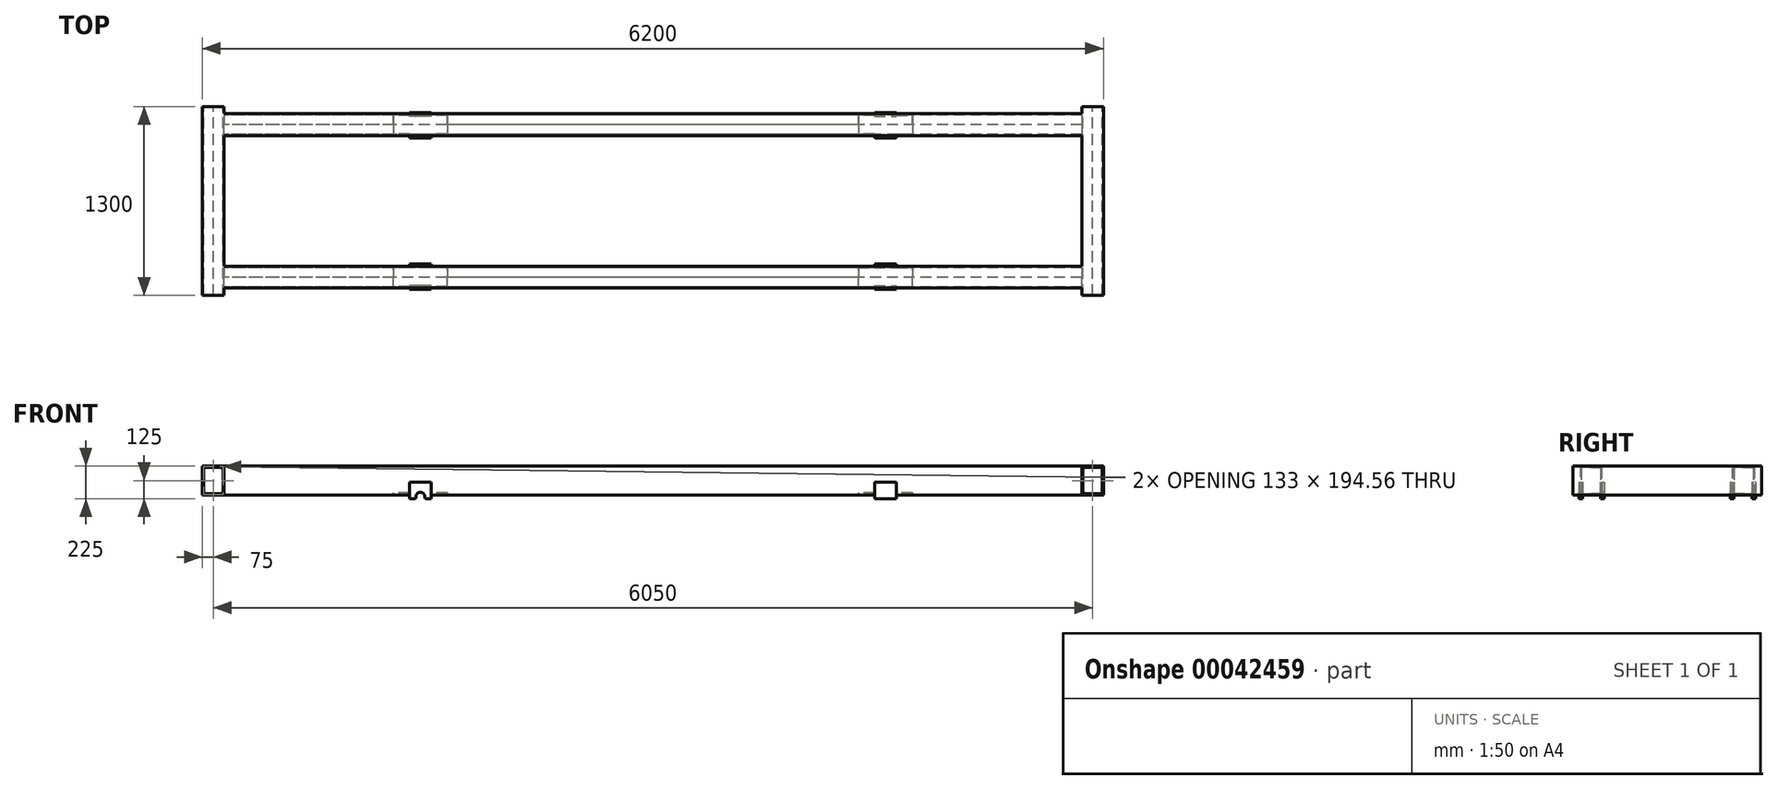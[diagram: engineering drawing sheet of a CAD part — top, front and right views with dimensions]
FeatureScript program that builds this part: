
annotation { "Feature Type Name" : "Feature", "Feature Type Description" : "" }
export const myFeature = defineFeature(function(context is Context, id is Id, definition is map)
    precondition{}
    {
        {
            assignVariable(context, id + "F0", {"variableType" : VariableType.LENGTH, "name" : "ProduktL", "lengthValue" : 6000 * mm});
        }
        {
            assignVariable(context, id + "F1", {"variableType" : VariableType.LENGTH, "name" : "ProduktB", "lengthValue" : 1300 * mm});
        }
        {
            assignVariable(context, id + "F2", {"variableType" : VariableType.LENGTH, "name" : "Spurweite", "lengthValue" : 1000 * mm});
        }
        {
            var Q0;
            Q0=qCreatedBy(makeId("Right.planeOp"),FACE);
            var sketch = newSketch(context, id + "F3", { "sketchPlane" : qUnion([Q0])});
            skLineSegment(sketch, "E0", {"start": v(-525, -69.6) * mm, "end": v(-525, -185.96) * mm, "construction": true});
            skLineSegment(sketch, "E1", {"start": v(-562.5, 183.56) * mm, "end": v(-562.5, -200) * mm, "construction": true});
            skLineSegment(sketch, "E2", {"start": v(-525, -100) * mm, "end": v(-600, -100) * mm, "construction": true});
            skLineSegment(sketch, "E3", {"start": v(-525, -2.72) * mm, "end": v(-525, 0) * mm});
            skPoint(sketch, "E3.startSnap0", {"position": v(-562.5, -8.22) * mm});
            skLineSegment(sketch, "E4", {"start": v(-525, 0) * mm, "end": v(-600, 0) * mm});
            skLineSegment(sketch, "E5", {"start": v(-600, 0) * mm, "end": v(-600, -200) * mm});
            skLineSegment(sketch, "E6", {"start": v(-600, -200) * mm, "end": v(-525, -200) * mm});
            skLineSegment(sketch, "E7", {"start": v(-525, -200) * mm, "end": v(-525, -197.28) * mm});
            skLineSegment(sketch, "E8", {"start": v(-530.48, -191.3) * mm, "end": v(-586.02, -186.44) * mm});
            skLineSegment(sketch, "E9", {"start": v(-591.5, -180.46) * mm, "end": v(-591.5, -19.54) * mm});
            skLineSegment(sketch, "E10", {"start": v(-586.02, -13.56) * mm, "end": v(-530.48, -8.7) * mm});
            skPoint(sketch, "E11.visualSharp", {"position": v(-591.5, -14.04) * mm});
            skArc(sketch, "E11.filletArc", {"start": v(-586.02, -13.56) * mm, "mid": v(-589.92, -15.48) * mm, "end": v(-591.5, -19.54) * mm});
            skPoint(sketch, "E12.visualSharp", {"position": v(-525, -8.22) * mm});
            skArc(sketch, "E12.filletArc", {"start": v(-530.48, -8.7) * mm, "mid": v(-526.58, -6.77) * mm, "end": v(-525, -2.72) * mm});
            skPoint(sketch, "E13.visualSharp", {"position": v(-525, -191.78) * mm});
            skArc(sketch, "E13.filletArc", {"start": v(-525, -197.28) * mm, "mid": v(-526.58, -193.23) * mm, "end": v(-530.48, -191.3) * mm});
            skPoint(sketch, "E14.visualSharp", {"position": v(-591.5, -185.96) * mm});
            skArc(sketch, "E14.filletArc", {"start": v(-591.5, -180.46) * mm, "mid": v(-589.92, -184.52) * mm, "end": v(-586.02, -186.44) * mm});
            skPoint(sketch, "E15", {"position": v(-600, -100) * mm});
            skPoint(sketch, "E16", {"position": v(-562.5, -200) * mm});
            skLineSegment(sketch, "E17", {"start": v(-562.5, 0) * mm, "end": v(-562.5, -11.5) * mm, "construction": true});
            skPoint(sketch, "E18", {"position": v(-591.5, -100) * mm});
            skLineSegment(sketch, "E19", {"start": v(-500, 0) * mm, "end": v(500, 0) * mm, "construction": true});
            skPoint(sketch, "E20", {"position": v(0, 0) * mm});
            skArc(sketch, "E21.MirrorCS", {"start": v(-525, -197.28) * mm, "mid": v(-523.42, -193.23) * mm, "end": v(-519.52, -191.3) * mm});
            skArc(sketch, "E22.MirrorCS", {"start": v(-458.5, -180.46) * mm, "mid": v(-460.08, -184.52) * mm, "end": v(-463.98, -186.44) * mm});
            skArc(sketch, "E23.MirrorCS", {"start": v(-463.98, -13.56) * mm, "mid": v(-460.08, -15.48) * mm, "end": v(-458.5, -19.54) * mm});
            skArc(sketch, "E24.MirrorCS", {"start": v(-519.52, -8.7) * mm, "mid": v(-523.42, -6.77) * mm, "end": v(-525, -2.72) * mm});
            skLineSegment(sketch, "E25.MirrorCS", {"start": v(-487.5, 0) * mm, "end": v(-487.5, -11.5) * mm, "construction": true});
            skPoint(sketch, "E26.MirrorP", {"position": v(-487.5, -8.22) * mm});
            skLineSegment(sketch, "E27.MirrorCS", {"start": v(-450, -200) * mm, "end": v(-525, -200) * mm});
            skLineSegment(sketch, "E28.MirrorCS", {"start": v(-458.5, -180.46) * mm, "end": v(-458.5, -19.54) * mm});
            skPoint(sketch, "E29.MirrorP", {"position": v(-458.5, -14.04) * mm});
            skLineSegment(sketch, "E30.MirrorCS", {"start": v(-525, -100) * mm, "end": v(-450, -100) * mm, "construction": true});
            skPoint(sketch, "E31.MirrorP", {"position": v(-450, -100) * mm});
            skLineSegment(sketch, "E32.MirrorCS", {"start": v(-519.52, -191.3) * mm, "end": v(-463.98, -186.44) * mm});
            skPoint(sketch, "E33.MirrorP", {"position": v(-458.5, -185.96) * mm});
            skPoint(sketch, "E34.MirrorP", {"position": v(-458.5, -100) * mm});
            skLineSegment(sketch, "E35.MirrorCS", {"start": v(-525, 0) * mm, "end": v(-450, 0) * mm});
            skLineSegment(sketch, "E36.MirrorCS", {"start": v(-463.98, -13.56) * mm, "end": v(-519.52, -8.7) * mm});
            skLineSegment(sketch, "E37.MirrorCS", {"start": v(-450, 0) * mm, "end": v(-450, -200) * mm});
            skPoint(sketch, "E38.MirrorP", {"position": v(-487.5, -200) * mm});
            skLineSegment(sketch, "E39.MirrorCS", {"start": v(525, -200) * mm, "end": v(525, -197.28) * mm});
            skArc(sketch, "E40.MirrorCS", {"start": v(525, -197.28) * mm, "mid": v(523.42, -193.23) * mm, "end": v(519.52, -191.3) * mm});
            skLineSegment(sketch, "E41.MirrorCS", {"start": v(525, -2.72) * mm, "end": v(525, 0) * mm});
            skArc(sketch, "E42.MirrorCS", {"start": v(525, -197.28) * mm, "mid": v(526.58, -193.23) * mm, "end": v(530.48, -191.3) * mm});
            skArc(sketch, "E43.MirrorCS", {"start": v(519.52, -8.7) * mm, "mid": v(523.42, -6.77) * mm, "end": v(525, -2.72) * mm});
            skArc(sketch, "E44.MirrorCS", {"start": v(530.48, -8.7) * mm, "mid": v(526.58, -6.77) * mm, "end": v(525, -2.72) * mm});
            skArc(sketch, "E45.MirrorCS", {"start": v(463.98, -13.56) * mm, "mid": v(460.08, -15.48) * mm, "end": v(458.5, -19.54) * mm});
            skArc(sketch, "E46.MirrorCS", {"start": v(591.5, -180.46) * mm, "mid": v(589.92, -184.52) * mm, "end": v(586.02, -186.44) * mm});
            skArc(sketch, "E47.MirrorCS", {"start": v(586.02, -13.56) * mm, "mid": v(589.92, -15.48) * mm, "end": v(591.5, -19.54) * mm});
            skArc(sketch, "E48.MirrorCS", {"start": v(458.5, -180.46) * mm, "mid": v(460.08, -184.52) * mm, "end": v(463.98, -186.44) * mm});
            skLineSegment(sketch, "E49.MirrorCS", {"start": v(586.02, -13.56) * mm, "end": v(530.48, -8.7) * mm});
            skPoint(sketch, "E50.MirrorP", {"position": v(525, -8.22) * mm});
            skPoint(sketch, "E51.MirrorP", {"position": v(525, -191.78) * mm});
            skLineSegment(sketch, "E52.MirrorCS", {"start": v(487.5, 0) * mm, "end": v(487.5, -11.5) * mm, "construction": true});
            skLineSegment(sketch, "E53.MirrorCS", {"start": v(562.5, 0) * mm, "end": v(562.5, -11.5) * mm, "construction": true});
            skLineSegment(sketch, "E54.MirrorCS", {"start": v(458.5, -180.46) * mm, "end": v(458.5, -19.54) * mm});
            skPoint(sketch, "E55.MirrorP", {"position": v(458.5, -14.04) * mm});
            skLineSegment(sketch, "E56.MirrorCS", {"start": v(525, 0) * mm, "end": v(600, 0) * mm});
            skPoint(sketch, "E57.MirrorP", {"position": v(591.5, -100) * mm});
            skLineSegment(sketch, "E58.MirrorCS", {"start": v(519.52, -191.3) * mm, "end": v(463.98, -186.44) * mm});
            skLineSegment(sketch, "E59.MirrorCS", {"start": v(525, 0) * mm, "end": v(450, 0) * mm});
            skLineSegment(sketch, "E60.MirrorCS", {"start": v(450, 0) * mm, "end": v(450, -200) * mm});
            skLineSegment(sketch, "E61.MirrorCS", {"start": v(525, -100) * mm, "end": v(450, -100) * mm, "construction": true});
            skPoint(sketch, "E62.MirrorP", {"position": v(458.5, -185.96) * mm});
            skPoint(sketch, "E63.MirrorP", {"position": v(591.5, -185.96) * mm});
            skPoint(sketch, "E64.MirrorP", {"position": v(562.5, -8.22) * mm});
            skLineSegment(sketch, "E65.MirrorCS", {"start": v(530.48, -191.3) * mm, "end": v(586.02, -186.44) * mm});
            skLineSegment(sketch, "E66.MirrorCS", {"start": v(600, 0) * mm, "end": v(600, -200) * mm});
            skLineSegment(sketch, "E67.MirrorCS", {"start": v(600, -200) * mm, "end": v(525, -200) * mm});
            skLineSegment(sketch, "E68.MirrorCS", {"start": v(591.5, -180.46) * mm, "end": v(591.5, -19.54) * mm});
            skPoint(sketch, "E69.MirrorP", {"position": v(450, -100) * mm});
            skLineSegment(sketch, "E70.MirrorCS", {"start": v(450, -200) * mm, "end": v(525, -200) * mm});
            skPoint(sketch, "E71.MirrorP", {"position": v(562.5, -200) * mm});
            skPoint(sketch, "E72.MirrorP", {"position": v(600, -100) * mm});
            skPoint(sketch, "E73.MirrorP", {"position": v(487.5, -200) * mm});
            skPoint(sketch, "E74.MirrorP", {"position": v(591.5, -14.04) * mm});
            skLineSegment(sketch, "E75.MirrorCS", {"start": v(525, -69.6) * mm, "end": v(525, -185.96) * mm, "construction": true});
            skLineSegment(sketch, "E76.MirrorCS", {"start": v(525, -100) * mm, "end": v(600, -100) * mm, "construction": true});
            skPoint(sketch, "E77.MirrorP", {"position": v(458.5, -100) * mm});
            skLineSegment(sketch, "E78.MirrorCS", {"start": v(463.98, -13.56) * mm, "end": v(519.52, -8.7) * mm});
            skPoint(sketch, "E79.MirrorP", {"position": v(487.5, -8.22) * mm});
            skSolve(sketch);
        }
        {
            var Q0;
            Q0=makeQuery(id+"F3.imprint","IMPRINT",FACE,{"disambiguationData":[TD([[makeQuery(id+"F3.imprint","IMPRINT",EDGE,{"derivedFrom":sQuery(id+"F3.wireOp",EDGE,"E4")}),1.0]])]});
            var Q1;
            Q1=makeQuery(id+"F3.imprint","IMPRINT",FACE,{"disambiguationData":[TD([[makeQuery(id+"F3.imprint","IMPRINT",EDGE,{"derivedFrom":sQuery(id+"F3.wireOp",EDGE,"E7")}),-1.0]])]});
            var Q2;
            Q2=makeQuery(id+"F3.imprint","IMPRINT",FACE,{"disambiguationData":[TD([[makeQuery(id+"F3.imprint","IMPRINT",EDGE,{"derivedFrom":sQuery(id+"F3.wireOp",EDGE,"E39.MirrorCS")}),1.0]])]});
            var Q3;
            Q3=makeQuery(id+"F3.imprint","IMPRINT",FACE,{"disambiguationData":[TD([[makeQuery(id+"F3.imprint","IMPRINT",EDGE,{"derivedFrom":sQuery(id+"F3.wireOp",EDGE,"E39.MirrorCS")}),-1.0]])]});
            extrude(context, id + "F4", {"entities" : qUnion([Q0, Q1, Q2, Q3]), "endBound" : BoundingType.SYMMETRIC, "depth" : getVariable(context, 'ProduktL'), "offsetDistance" : 25 * mm});
        }
        {
            var Q0;
            Q0=makeQuery(id+"F4.opExtrude","SWEPT_FACE",FACE,{"disambiguationData":[OSD([sQuery(id+"F3.wireOp",EDGE,"E5")])]});
            var sketch = newSketch(context, id + "F5", { "sketchPlane" : qUnion([Q0])});
            skLineSegment(sketch, "E80", {"start": v(-3000, 0) * mm, "end": v(3000, 0) * mm, "construction": true});
            skPoint(sketch, "E81", {"position": v(0, 0) * mm});
            skLineSegment(sketch, "E82", {"start": v(-3000, 0) * mm, "end": v(-3100, 0) * mm, "construction": true});
            skLineSegment(sketch, "E83", {"start": v(3000, 0) * mm, "end": v(3100, 0) * mm, "construction": true});
            skLineSegment(sketch, "E84.bottom", {"start": v(-3100, 0) * mm, "end": v(-3025, 0) * mm});
            skLineSegment(sketch, "E84.top", {"start": v(-3100, -200) * mm, "end": v(-3025, -200) * mm});
            skLineSegment(sketch, "E84.left", {"start": v(-3100, 0) * mm, "end": v(-3100, -200) * mm});
            skLineSegment(sketch, "E84.right", {"start": v(-3025, 0) * mm, "end": v(-3025, -200) * mm});
            skLineSegment(sketch, "E85.bottom", {"start": v(-3025, 0) * mm, "end": v(-2950, 0) * mm});
            skLineSegment(sketch, "E85.top", {"start": v(-3025, -200) * mm, "end": v(-2950, -200) * mm});
            skLineSegment(sketch, "E85.right", {"start": v(-2950, 0) * mm, "end": v(-2950, -200) * mm});
            skLineSegment(sketch, "E86.MirrorCS", {"start": v(3025, 0) * mm, "end": v(3025, -200) * mm});
            skLineSegment(sketch, "E87.MirrorCS", {"start": v(3100, 0) * mm, "end": v(3025, 0) * mm});
            skLineSegment(sketch, "E88.MirrorCS", {"start": v(3100, 0) * mm, "end": v(3100, -200) * mm});
            skLineSegment(sketch, "E89.MirrorCS", {"start": v(3025, 0) * mm, "end": v(2950, 0) * mm});
            skLineSegment(sketch, "E90.MirrorCS", {"start": v(2950, 0) * mm, "end": v(2950, -200) * mm});
            skLineSegment(sketch, "E91.MirrorCS", {"start": v(3025, -200) * mm, "end": v(2950, -200) * mm});
            skLineSegment(sketch, "E92.MirrorCS", {"start": v(3100, -200) * mm, "end": v(3025, -200) * mm});
            skSolve(sketch);
        }
        {
            var Q0;
            Q0=makeQuery(id+"F5.imprint","IMPRINT",FACE,{"disambiguationData":[TD([[makeQuery(id+"F5.imprint","IMPRINT",EDGE,{"derivedFrom":sQuery(id+"F5.wireOp",EDGE,"E84.bottom")}),-1.0]])]});
            var Q1;
            {var subQ3=sQuery(id+"F5.wireOp",EDGE,"E85.right");Q1=makeQuery(id+"F5.imprint","IMPRINT",FACE,{"disambiguationData":[TD([[makeQuery(id+"F5.imprint","IMPRINT",EDGE,{"derivedFrom":subQ3}),-1.0]])]});}
            var Q2;
            {var subQ0=sQuery(id+"F5.wireOp",EDGE,"E86.MirrorCS");Q2=makeQuery(id+"F5.imprint","IMPRINT",FACE,{"disambiguationData":[TD([[makeQuery(id+"F5.imprint","IMPRINT",EDGE,{"derivedFrom":subQ0}),-1.0]])]});}
            var Q3;
            {var subQ3=sQuery(id+"F5.wireOp",EDGE,"E90.MirrorCS");Q3=makeQuery(id+"F5.imprint","IMPRINT",FACE,{"disambiguationData":[TD([[makeQuery(id+"F5.imprint","IMPRINT",EDGE,{"derivedFrom":subQ3}),1.0]])]});}
            var Q4;
            Q4=makeQuery(id+"F5.imprint","IMPRINT",FACE,{"disambiguationData":[TD([[makeQuery(id+"F5.imprint","IMPRINT",EDGE,{"derivedFrom":sQuery(id+"F5.wireOp",EDGE,"E87.MirrorCS")}),1.0]])]});
            var Q5;
            {var subQ2=sQuery(id+"F5.wireOp",EDGE,"E84.right");Q5=makeQuery(id+"F5.imprint","IMPRINT",FACE,{"disambiguationData":[TD([[makeQuery(id+"F5.imprint","IMPRINT",EDGE,{"derivedFrom":subQ2}),1.0]])]});}
            extrude(context, id + "F6", {"entities" : qUnion([Q0, Q1, Q2, Q3, Q4, Q5]), "operationType" : NewBodyOperationType.REMOVE, "endBound" : BoundingType.THROUGH_ALL, "oppositeDirection" : true, "depth" : 25 * mm, "offsetDistance" : 25 * mm});
        }
        {
            var Q0;
            Q0=qCreatedBy(makeId("Front.planeOp"),FACE);
            var sketch = newSketch(context, id + "F7", { "sketchPlane" : qUnion([Q0])});
            skLineSegment(sketch, "E93.0", {"start": v(-2950, -200) * mm, "end": v(-2950, 0) * mm});
            skLineSegment(sketch, "E94", {"start": v(-2950, 0) * mm, "end": v(-3025, 0) * mm});
            skLineSegment(sketch, "E95", {"start": v(-3025, 0) * mm, "end": v(-3025, -2.72) * mm});
            skLineSegment(sketch, "E96", {"start": v(-3019.52, -8.7) * mm, "end": v(-2969, -13.12) * mm});
            skLineSegment(sketch, "E97", {"start": v(-2958.5, -24.57) * mm, "end": v(-2958.5, -175.43) * mm});
            skLineSegment(sketch, "E98", {"start": v(-2969, -186.88) * mm, "end": v(-3019.52, -191.3) * mm});
            skLineSegment(sketch, "E99", {"start": v(-3025, -197.28) * mm, "end": v(-3025, -200) * mm});
            skLineSegment(sketch, "E100", {"start": v(-3025, -200) * mm, "end": v(-2950, -200) * mm});
            skPoint(sketch, "E101.visualSharp", {"position": v(-3025, -8.22) * mm});
            skArc(sketch, "E101.filletArc", {"start": v(-3025, -2.72) * mm, "mid": v(-3023.42, -6.77) * mm, "end": v(-3019.52, -8.7) * mm});
            skPoint(sketch, "E102.visualSharp", {"position": v(-2958.5, -14.04) * mm});
            skArc(sketch, "E102.filletArc", {"start": v(-2958.5, -24.57) * mm, "mid": v(-2961.52, -16.8) * mm, "end": v(-2969, -13.12) * mm});
            skPoint(sketch, "E103.visualSharp", {"position": v(-2958.5, -185.96) * mm});
            skArc(sketch, "E103.filletArc", {"start": v(-2969, -186.88) * mm, "mid": v(-2961.52, -183.2) * mm, "end": v(-2958.5, -175.43) * mm});
            skPoint(sketch, "E104.visualSharp", {"position": v(-3025, -191.78) * mm});
            skArc(sketch, "E104.filletArc", {"start": v(-3019.52, -191.3) * mm, "mid": v(-3023.42, -193.23) * mm, "end": v(-3025, -197.28) * mm});
            skLineSegment(sketch, "E105", {"start": v(-2987.5, 0) * mm, "end": v(-2987.5, -11.5) * mm, "construction": true});
            skLineSegment(sketch, "E106", {"start": v(-3025, 9.58) * mm, "end": v(-3025, 59.58) * mm, "construction": true});
            skArc(sketch, "E107.MirrorCS", {"start": v(-3025, -2.72) * mm, "mid": v(-3026.58, -6.77) * mm, "end": v(-3030.48, -8.7) * mm});
            skArc(sketch, "E108.MirrorCS", {"start": v(-3030.48, -191.3) * mm, "mid": v(-3026.58, -193.23) * mm, "end": v(-3025, -197.28) * mm});
            skArc(sketch, "E109.MirrorCS", {"start": v(-3081, -186.88) * mm, "mid": v(-3088.48, -183.2) * mm, "end": v(-3091.5, -175.43) * mm});
            skLineSegment(sketch, "E110.MirrorCS", {"start": v(-3062.5, 0) * mm, "end": v(-3062.5, -11.5) * mm, "construction": true});
            skArc(sketch, "E111.MirrorCS", {"start": v(-3091.5, -24.57) * mm, "mid": v(-3088.48, -16.8) * mm, "end": v(-3081, -13.12) * mm});
            skLineSegment(sketch, "E112.MirrorCS", {"start": v(-3025, -200) * mm, "end": v(-3100, -200) * mm});
            skLineSegment(sketch, "E113.MirrorCS", {"start": v(-3030.48, -8.7) * mm, "end": v(-3081, -13.12) * mm});
            skLineSegment(sketch, "E114.MirrorCS", {"start": v(-3100, -200) * mm, "end": v(-3100, 0) * mm});
            skLineSegment(sketch, "E115.MirrorCS", {"start": v(-3081, -186.88) * mm, "end": v(-3030.48, -191.3) * mm});
            skLineSegment(sketch, "E116.MirrorCS", {"start": v(-3100, 0) * mm, "end": v(-3025, 0) * mm});
            skPoint(sketch, "E117.MirrorP", {"position": v(-3091.5, -185.96) * mm});
            skLineSegment(sketch, "E118.MirrorCS", {"start": v(-3091.5, -24.57) * mm, "end": v(-3091.5, -175.43) * mm});
            skPoint(sketch, "E119.MirrorP", {"position": v(-3091.5, -14.04) * mm});
            skLineSegment(sketch, "E120.MirrorCS", {"start": v(3025, 0) * mm, "end": v(3025, -2.72) * mm});
            skArc(sketch, "E121.MirrorCS", {"start": v(3025, -2.72) * mm, "mid": v(3026.58, -6.77) * mm, "end": v(3030.48, -8.7) * mm});
            skArc(sketch, "E122.MirrorCS", {"start": v(3025, -2.72) * mm, "mid": v(3023.42, -6.77) * mm, "end": v(3019.52, -8.7) * mm});
            skLineSegment(sketch, "E123.MirrorCS", {"start": v(3025, -197.28) * mm, "end": v(3025, -200) * mm});
            skArc(sketch, "E124.MirrorCS", {"start": v(3030.48, -191.3) * mm, "mid": v(3026.58, -193.23) * mm, "end": v(3025, -197.28) * mm});
            skArc(sketch, "E125.MirrorCS", {"start": v(3019.52, -191.3) * mm, "mid": v(3023.42, -193.23) * mm, "end": v(3025, -197.28) * mm});
            skArc(sketch, "E126.MirrorCS", {"start": v(3081, -186.88) * mm, "mid": v(3088.48, -183.2) * mm, "end": v(3091.5, -175.43) * mm});
            skLineSegment(sketch, "E127.MirrorCS", {"start": v(3062.5, 0) * mm, "end": v(3062.5, -11.5) * mm, "construction": true});
            skLineSegment(sketch, "E128.MirrorCS", {"start": v(2969, -186.88) * mm, "end": v(3019.52, -191.3) * mm});
            skArc(sketch, "E129.MirrorCS", {"start": v(3091.5, -24.57) * mm, "mid": v(3088.48, -16.8) * mm, "end": v(3081, -13.12) * mm});
            skLineSegment(sketch, "E130.MirrorCS", {"start": v(3025, -200) * mm, "end": v(3100, -200) * mm});
            skLineSegment(sketch, "E131.MirrorCS", {"start": v(3019.52, -8.7) * mm, "end": v(2969, -13.12) * mm});
            skLineSegment(sketch, "E132.MirrorCS", {"start": v(2950, 0) * mm, "end": v(3025, 0) * mm});
            skLineSegment(sketch, "E133.MirrorCS", {"start": v(3030.48, -8.7) * mm, "end": v(3081, -13.12) * mm});
            skLineSegment(sketch, "E134.MirrorCS", {"start": v(3081, -186.88) * mm, "end": v(3030.48, -191.3) * mm});
            skArc(sketch, "E135.MirrorCS", {"start": v(2969, -186.88) * mm, "mid": v(2961.52, -183.2) * mm, "end": v(2958.5, -175.43) * mm});
            skLineSegment(sketch, "E136.MirrorCS", {"start": v(3100, 0) * mm, "end": v(3025, 0) * mm});
            skArc(sketch, "E137.MirrorCS", {"start": v(2958.5, -24.57) * mm, "mid": v(2961.52, -16.8) * mm, "end": v(2969, -13.12) * mm});
            skLineSegment(sketch, "E138.MirrorCS", {"start": v(3025, -200) * mm, "end": v(2950, -200) * mm});
            skLineSegment(sketch, "E139.MirrorCS", {"start": v(2987.5, 0) * mm, "end": v(2987.5, -11.5) * mm, "construction": true});
            skPoint(sketch, "E140.MirrorP", {"position": v(3025, -8.22) * mm});
            skPoint(sketch, "E141.MirrorP", {"position": v(3025, -191.78) * mm});
            skPoint(sketch, "E142.MirrorP", {"position": v(2958.5, -185.96) * mm});
            skPoint(sketch, "E143.MirrorP", {"position": v(2958.5, -14.04) * mm});
            skLineSegment(sketch, "E144.MirrorCS", {"start": v(2958.5, -24.57) * mm, "end": v(2958.5, -175.43) * mm});
            skLineSegment(sketch, "E145.MirrorCS", {"start": v(2950, -200) * mm, "end": v(2950, 0) * mm});
            skLineSegment(sketch, "E146.MirrorCS", {"start": v(3091.5, -24.57) * mm, "end": v(3091.5, -175.43) * mm});
            skLineSegment(sketch, "E147.MirrorCS", {"start": v(3100, -200) * mm, "end": v(3100, 0) * mm});
            skPoint(sketch, "E148.MirrorP", {"position": v(3091.5, -185.96) * mm});
            skPoint(sketch, "E149.MirrorP", {"position": v(3091.5, -14.04) * mm});
            skSolve(sketch);
        }
        {
            var Q0;
            Q0=makeQuery(id+"F7.imprint","IMPRINT",FACE,{"disambiguationData":[TD([[makeQuery(id+"F7.imprint","IMPRINT",EDGE,{"derivedFrom":sQuery(id+"F7.wireOp",EDGE,"E99")}),-1.0]])]});
            var Q1;
            Q1=makeQuery(id+"F7.imprint","IMPRINT",FACE,{"disambiguationData":[TD([[makeQuery(id+"F7.imprint","IMPRINT",EDGE,{"derivedFrom":sQuery(id+"F7.wireOp",EDGE,"E93.0")}),1.0]])]});
            var Q2;
            Q2=makeQuery(id+"F7.imprint","IMPRINT",FACE,{"disambiguationData":[TD([[makeQuery(id+"F7.imprint","IMPRINT",EDGE,{"derivedFrom":sQuery(id+"F7.wireOp",EDGE,"E120.MirrorCS")}),-1.0]])]});
            var Q3;
            Q3=makeQuery(id+"F7.imprint","IMPRINT",FACE,{"disambiguationData":[TD([[makeQuery(id+"F7.imprint","IMPRINT",EDGE,{"derivedFrom":sQuery(id+"F7.wireOp",EDGE,"E120.MirrorCS")}),1.0]])]});
            extrude(context, id + "F8", {"entities" : qUnion([Q0, Q1, Q2, Q3]), "operationType" : NewBodyOperationType.ADD, "endBound" : BoundingType.SYMMETRIC, "depth" : getVariable(context, 'ProduktB'), "offsetDistance" : 25 * mm});
        }
        {
            var Q0;
            Q0=qCreatedBy(makeId("Front.planeOp"),FACE);
            var sketch = newSketch(context, id + "F9", { "sketchPlane" : qUnion([Q0])});
            skLineSegment(sketch, "E150", {"start": v(-1600, 0) * mm, "end": v(1600, 0) * mm, "construction": true});
            skPoint(sketch, "E151", {"position": v(0, 0) * mm});
            skLineSegment(sketch, "E152.bottom", {"start": v(-1675, -110) * mm, "end": v(-1525, -110) * mm});
            skLineSegment(sketch, "E152.top", {"start": v(-1675, -225) * mm, "end": v(-1525, -225) * mm});
            skLineSegment(sketch, "E152.left", {"start": v(-1675, -110) * mm, "end": v(-1675, -225) * mm});
            skLineSegment(sketch, "E152.right", {"start": v(-1525, -110) * mm, "end": v(-1525, -225) * mm});
            skLineSegment(sketch, "E153", {"start": v(-1600, 0) * mm, "end": v(-1600, -225) * mm, "construction": true});
            skLineSegment(sketch, "E154.MirrorCS", {"start": v(1525, -110) * mm, "end": v(1525, -225) * mm});
            skLineSegment(sketch, "E155.MirrorCS", {"start": v(1675, -225) * mm, "end": v(1525, -225) * mm});
            skLineSegment(sketch, "E156.MirrorCS", {"start": v(1675, -110) * mm, "end": v(1525, -110) * mm});
            skLineSegment(sketch, "E157.MirrorCS", {"start": v(1600, 0) * mm, "end": v(1600, -225) * mm, "construction": true});
            skLineSegment(sketch, "E158.MirrorCS", {"start": v(1675, -110) * mm, "end": v(1675, -225) * mm});
            skSolve(sketch);
        }
        {
            var Q0;
            Q0=makeQuery(id+"F9.imprint","IMPRINT",FACE,{"disambiguationData":[TD([[makeQuery(id+"F9.imprint","IMPRINT",EDGE,{"derivedFrom":sQuery(id+"F9.wireOp",EDGE,"E152.bottom")}),-1.0]])]});
            var Q1;
            Q1=makeQuery(id+"F9.imprint","IMPRINT",FACE,{"disambiguationData":[TD([[makeQuery(id+"F9.imprint","IMPRINT",EDGE,{"derivedFrom":sQuery(id+"F9.wireOp",EDGE,"E154.MirrorCS")}),1.0]])]});
            var Q2;
            Q2=makeQuery(id+"F4.opExtrude","SWEPT_FACE",FACE,{"disambiguationData":[OSD([sQuery(id+"F3.wireOp",EDGE,"E5")])]});
            var Q3;
            Q3=makeQuery(id+"F4.opExtrude","SWEPT_BODY",BODY,{"disambiguationData":[OSD([sQuery(id+"F3.wireOp",EDGE,"E4"),sQuery(id+"F3.wireOp",EDGE,"E5"),sQuery(id+"F3.wireOp",EDGE,"E6"),sQuery(id+"F3.wireOp",EDGE,"E8"),sQuery(id+"F3.wireOp",EDGE,"E9"),sQuery(id+"F3.wireOp",EDGE,"E10"),sQuery(id+"F3.wireOp",EDGE,"E11.filletArc"),sQuery(id+"F3.wireOp",EDGE,"E12.filletArc"),sQuery(id+"F3.wireOp",EDGE,"E13.filletArc"),sQuery(id+"F3.wireOp",EDGE,"E14.filletArc"),sQuery(id+"F3.wireOp",EDGE,"E21.MirrorCS"),sQuery(id+"F3.wireOp",EDGE,"E22.MirrorCS"),sQuery(id+"F3.wireOp",EDGE,"E23.MirrorCS"),sQuery(id+"F3.wireOp",EDGE,"E24.MirrorCS"),sQuery(id+"F3.wireOp",EDGE,"E27.MirrorCS"),sQuery(id+"F3.wireOp",EDGE,"E28.MirrorCS"),sQuery(id+"F3.wireOp",EDGE,"E32.MirrorCS"),sQuery(id+"F3.wireOp",EDGE,"E35.MirrorCS"),sQuery(id+"F3.wireOp",EDGE,"E36.MirrorCS"),sQuery(id+"F3.wireOp",EDGE,"E37.MirrorCS")])]});
            var Q4;
            Q4=makeQuery(id+"F4.opExtrude","SWEPT_FACE",FACE,{"disambiguationData":[OSD([sQuery(id+"F3.wireOp",EDGE,"E66.MirrorCS")])]});
            extrude(context, id + "F10", {"entities" : qUnion([Q0, Q1]), "operationType" : NewBodyOperationType.REMOVE, "endBound" : BoundingType.UP_TO_SURFACE, "depth" : 25 * mm, "endBoundEntityFace" : qUnion([Q2]), "endBoundEntityBody" : qUnion([Q3]), "offsetDistance" : 25 * mm, "hasSecondDirection" : true, "secondDirectionBound" : SecondDirectionBoundingType.UP_TO_SURFACE, "secondDirectionOppositeDirection" : true, "secondDirectionDepth" : 25 * mm, "secondDirectionBoundEntityFace" : qUnion([Q4])});
        }
        {
            var Q0;
            Q0=makeQuery(id+"F10.boolean.opBoolean","SPLIT",FACE,{"disambiguationData":[TD([makeQuery(id+"F4.opExtrude","SWEPT_FACE",FACE,{"disambiguationData":[OSD([sQuery(id+"F3.wireOp",EDGE,"E5")])]}),makeQuery(id+"F4.opExtrude","SWEPT_FACE",FACE,{"disambiguationData":[OSD([sQuery(id+"F3.wireOp",EDGE,"E37.MirrorCS")])]}),makeQuery(id+"F10.opExtrude","SWEPT_FACE",FACE,{"disambiguationData":[OSD([sQuery(id+"F9.wireOp",EDGE,"E152.right")])]}),makeQuery(id+"F10.opExtrude","SWEPT_FACE",FACE,{"disambiguationData":[OSD([sQuery(id+"F9.wireOp",EDGE,"E154.MirrorCS")])]})])],"derivedFrom":makeQuery(id+"F8.boolean.opBoolean","MERGE",FACE,{"derivedFrom":[makeQuery(id+"F4.opExtrude","SWEPT_FACE",FACE,{"disambiguationData":[OSD([sQuery(id+"F3.wireOp",EDGE,"E6"),sQuery(id+"F3.wireOp",EDGE,"E27.MirrorCS")])]}),makeQuery(id+"F4.opExtrude","SWEPT_FACE",FACE,{"disambiguationData":[OSD([sQuery(id+"F3.wireOp",EDGE,"E67.MirrorCS"),sQuery(id+"F3.wireOp",EDGE,"E70.MirrorCS")])]}),makeQuery(id+"F8.opExtrude","SWEPT_FACE",FACE,{"disambiguationData":[OSD([sQuery(id+"F7.wireOp",EDGE,"E100"),sQuery(id+"F7.wireOp",EDGE,"E112.MirrorCS")])]}),makeQuery(id+"F8.opExtrude","SWEPT_FACE",FACE,{"disambiguationData":[OSD([sQuery(id+"F7.wireOp",EDGE,"E130.MirrorCS"),sQuery(id+"F7.wireOp",EDGE,"E138.MirrorCS")])]})]})});
            var sketch = newSketch(context, id + "F11", { "sketchPlane" : qUnion([Q0])});
            skLineSegment(sketch, "E159.0", {"start": v(1525, 600) * mm, "end": v(1525, 450) * mm});
            skLineSegment(sketch, "E160.0", {"start": v(1675, 600) * mm, "end": v(1675, 450) * mm});
            skLineSegment(sketch, "E161.0", {"start": v(2950, 525) * mm, "end": v(-2950, 525) * mm});
            skLineSegment(sketch, "E162.bottom", {"start": v(1415, 590) * mm, "end": v(1785, 590) * mm});
            skLineSegment(sketch, "E162.top", {"start": v(1415, 460) * mm, "end": v(1785, 460) * mm});
            skLineSegment(sketch, "E162.left", {"start": v(1415, 590) * mm, "end": v(1415, 460) * mm});
            skLineSegment(sketch, "E162.right", {"start": v(1785, 590) * mm, "end": v(1785, 460) * mm});
            skLineSegment(sketch, "E163", {"start": v(1675, 600) * mm, "end": v(1525, 600) * mm, "construction": true});
            skLineSegment(sketch, "E164", {"start": v(1600, 600) * mm, "end": v(1600, 450) * mm, "construction": true});
            skLineSegment(sketch, "E165.MirrorCS", {"start": v(-1415, 590) * mm, "end": v(-1415, 460) * mm});
            skLineSegment(sketch, "E166.MirrorCS", {"start": v(-1415, 590) * mm, "end": v(-1785, 590) * mm});
            skLineSegment(sketch, "E167.MirrorCS", {"start": v(-1415, 460) * mm, "end": v(-1785, 460) * mm});
            skLineSegment(sketch, "E168.MirrorCS", {"start": v(-1785, 590) * mm, "end": v(-1785, 460) * mm});
            skLineSegment(sketch, "E169.MirrorCS", {"start": v(-1785, -590) * mm, "end": v(-1785, -460) * mm});
            skLineSegment(sketch, "E170.MirrorCS", {"start": v(-1415, -590) * mm, "end": v(-1785, -590) * mm});
            skLineSegment(sketch, "E171.MirrorCS", {"start": v(-1415, -590) * mm, "end": v(-1415, -460) * mm});
            skLineSegment(sketch, "E172.MirrorCS", {"start": v(-1415, -460) * mm, "end": v(-1785, -460) * mm});
            skLineSegment(sketch, "E173.MirrorCS", {"start": v(1415, -590) * mm, "end": v(1415, -460) * mm});
            skLineSegment(sketch, "E174.MirrorCS", {"start": v(1415, -460) * mm, "end": v(1785, -460) * mm});
            skLineSegment(sketch, "E175.MirrorCS", {"start": v(1785, -590) * mm, "end": v(1785, -460) * mm});
            skLineSegment(sketch, "E176.MirrorCS", {"start": v(1415, -590) * mm, "end": v(1785, -590) * mm});
            skSolve(sketch);
        }
        {
            var Q0;
            Q0=makeQuery(id+"F11.imprint","IMPRINT",FACE,{"disambiguationData":[TD([[makeQuery(id+"F11.imprint","IMPRINT",EDGE,{"derivedFrom":sQuery(id+"F11.wireOp",EDGE,"E169.MirrorCS")}),-1.0]])]});
            var Q1;
            Q1=makeQuery(id+"F11.imprint","IMPRINT",FACE,{"disambiguationData":[TD([[makeQuery(id+"F11.imprint","IMPRINT",EDGE,{"derivedFrom":sQuery(id+"F11.wireOp",EDGE,"E173.MirrorCS")}),-1.0]])]});
            var Q2;
            {var subQ0=sQuery(id+"F11.wireOp",EDGE,"E168.MirrorCS");var subQ5=sQuery(id+"F11.wireOp",EDGE,"E166.MirrorCS");var subQ6=makeQuery(id+"F11.imprint","INTERSECT",VERTEX,{"derivedFrom":[subQ5,subQ0]});Q2=makeQuery(id+"F11.imprint","IMPRINT",FACE,{"disambiguationData":[TD([[makeQuery(id+"F11.imprint","IMPRINT",EDGE,{"disambiguationData":[TD([[subQ6,-1.0]])],"derivedFrom":subQ0}),1.0]])]});}
            var Q3;
            {var subQ0=sQuery(id+"F11.wireOp",EDGE,"E165.MirrorCS");var subQ5=sQuery(id+"F11.wireOp",EDGE,"E166.MirrorCS");var subQ6=makeQuery(id+"F11.imprint","INTERSECT",VERTEX,{"derivedFrom":[subQ0,subQ5]});Q3=makeQuery(id+"F11.imprint","IMPRINT",FACE,{"disambiguationData":[TD([[makeQuery(id+"F11.imprint","IMPRINT",EDGE,{"disambiguationData":[TD([[subQ6,-1.0]])],"derivedFrom":subQ0}),-1.0]])]});}
            var Q4;
            {var subQ0=sQuery(id+"F11.wireOp",EDGE,"E168.MirrorCS");var subQ5=sQuery(id+"F11.wireOp",EDGE,"E167.MirrorCS");var subQ6=makeQuery(id+"F11.imprint","INTERSECT",VERTEX,{"derivedFrom":[subQ5,subQ0]});Q4=makeQuery(id+"F11.imprint","IMPRINT",FACE,{"disambiguationData":[TD([[makeQuery(id+"F11.imprint","IMPRINT",EDGE,{"disambiguationData":[TD([[subQ6,1.0]])],"derivedFrom":subQ0}),1.0]])]});}
            var Q5;
            {var subQ0=sQuery(id+"F11.wireOp",EDGE,"E165.MirrorCS");var subQ5=sQuery(id+"F11.wireOp",EDGE,"E167.MirrorCS");var subQ6=makeQuery(id+"F11.imprint","INTERSECT",VERTEX,{"derivedFrom":[subQ0,subQ5]});Q5=makeQuery(id+"F11.imprint","IMPRINT",FACE,{"disambiguationData":[TD([[makeQuery(id+"F11.imprint","IMPRINT",EDGE,{"disambiguationData":[TD([[subQ6,1.0]])],"derivedFrom":subQ0}),-1.0]])]});}
            var Q6;
            {var subQ0=sQuery(id+"F11.wireOp",EDGE,"E162.bottom");var subQ1=sQuery(id+"F11.wireOp",EDGE,"E159.0");var subQ2=makeQuery(id+"F11.imprint","INTERSECT",VERTEX,{"derivedFrom":[subQ1,subQ0]});Q6=makeQuery(id+"F11.imprint","IMPRINT",FACE,{"disambiguationData":[TD([[makeQuery(id+"F11.imprint","IMPRINT",EDGE,{"disambiguationData":[TD([[subQ2,-1.0]])],"derivedFrom":subQ1}),-1.0]])]});}
            var Q7;
            {var subQ0=sQuery(id+"F11.wireOp",EDGE,"E162.bottom");var subQ1=sQuery(id+"F11.wireOp",EDGE,"E159.0");var subQ2=makeQuery(id+"F11.imprint","INTERSECT",VERTEX,{"derivedFrom":[subQ1,subQ0]});Q7=makeQuery(id+"F11.imprint","IMPRINT",FACE,{"disambiguationData":[TD([[makeQuery(id+"F11.imprint","IMPRINT",EDGE,{"disambiguationData":[TD([[subQ2,-1.0]])],"derivedFrom":subQ1}),1.0]])]});}
            var Q8;
            {var subQ0=sQuery(id+"F11.wireOp",EDGE,"E162.bottom");var subQ1=sQuery(id+"F11.wireOp",EDGE,"E160.0");var subQ2=makeQuery(id+"F11.imprint","INTERSECT",VERTEX,{"derivedFrom":[subQ1,subQ0]});Q8=makeQuery(id+"F11.imprint","IMPRINT",FACE,{"disambiguationData":[TD([[makeQuery(id+"F11.imprint","IMPRINT",EDGE,{"disambiguationData":[TD([[subQ2,-1.0]])],"derivedFrom":subQ1}),1.0]])]});}
            var Q9;
            {var subQ0=sQuery(id+"F11.wireOp",EDGE,"E162.top");var subQ1=sQuery(id+"F11.wireOp",EDGE,"E160.0");var subQ2=makeQuery(id+"F11.imprint","INTERSECT",VERTEX,{"derivedFrom":[subQ1,subQ0]});Q9=makeQuery(id+"F11.imprint","IMPRINT",FACE,{"disambiguationData":[TD([[makeQuery(id+"F11.imprint","IMPRINT",EDGE,{"disambiguationData":[TD([[subQ2,1.0]])],"derivedFrom":subQ1}),1.0]])]});}
            var Q10;
            {var subQ0=sQuery(id+"F11.wireOp",EDGE,"E162.top");var subQ1=sQuery(id+"F11.wireOp",EDGE,"E159.0");var subQ2=makeQuery(id+"F11.imprint","INTERSECT",VERTEX,{"derivedFrom":[subQ1,subQ0]});Q10=makeQuery(id+"F11.imprint","IMPRINT",FACE,{"disambiguationData":[TD([[makeQuery(id+"F11.imprint","IMPRINT",EDGE,{"disambiguationData":[TD([[subQ2,1.0]])],"derivedFrom":subQ1}),1.0]])]});}
            var Q11;
            {var subQ0=sQuery(id+"F11.wireOp",EDGE,"E162.top");var subQ1=sQuery(id+"F11.wireOp",EDGE,"E159.0");var subQ2=makeQuery(id+"F11.imprint","INTERSECT",VERTEX,{"derivedFrom":[subQ1,subQ0]});Q11=makeQuery(id+"F11.imprint","IMPRINT",FACE,{"disambiguationData":[TD([[makeQuery(id+"F11.imprint","IMPRINT",EDGE,{"disambiguationData":[TD([[subQ2,1.0]])],"derivedFrom":subQ1}),-1.0]])]});}
            extrude(context, id + "F12", {"entities" : qUnion([Q0, Q1, Q2, Q3, Q4, Q5, Q6, Q7, Q8, Q9, Q10, Q11]), "operationType" : NewBodyOperationType.REMOVE, "oppositeDirection" : true, "depth" : 50 * mm, "offsetDistance" : 25 * mm});
        }
        {
            var Q0;
            Q0=makeQuery(id+"F9.imprint","IMPRINT",FACE,{"disambiguationData":[TD([[makeQuery(id+"F9.imprint","IMPRINT",EDGE,{"derivedFrom":sQuery(id+"F9.wireOp",EDGE,"E152.bottom")}),-1.0]])]});
            var Q1;
            Q1=makeQuery(id+"F9.imprint","IMPRINT",FACE,{"disambiguationData":[TD([[makeQuery(id+"F9.imprint","IMPRINT",EDGE,{"derivedFrom":sQuery(id+"F9.wireOp",EDGE,"E154.MirrorCS")}),1.0]])]});
            extrude(context, id + "F13", {"entities" : qUnion([Q0, Q1]), "endBound" : BoundingType.SYMMETRIC, "depth" : getVariable(context, 'Spurweite'), "offsetDistance" : 25 * mm});
        }
        {
            var Q0;
            Q0=makeQuery(id+"F13.opExtrude","CAP_FACE",FACE,{"disambiguationData":[OSD([sQuery(id+"F9.wireOp",EDGE,"E152.bottom"),sQuery(id+"F9.wireOp",EDGE,"E152.top"),sQuery(id+"F9.wireOp",EDGE,"E152.left"),sQuery(id+"F9.wireOp",EDGE,"E152.right")])],"isStart":false});
            var Q1;
            Q1=makeQuery(id+"F13.opExtrude","CAP_FACE",FACE,{"disambiguationData":[OSD([sQuery(id+"F9.wireOp",EDGE,"E154.MirrorCS"),sQuery(id+"F9.wireOp",EDGE,"E155.MirrorCS"),sQuery(id+"F9.wireOp",EDGE,"E156.MirrorCS"),sQuery(id+"F9.wireOp",EDGE,"E158.MirrorCS")])],"isStart":false});
            extrude(context, id + "F14", {"entities" : qUnion([Q0, Q1]), "operationType" : NewBodyOperationType.ADD, "depth" : 107.5 * mm, "offsetDistance" : 25 * mm});
        }
        {
            var Q0;
            Q0=makeQuery(id+"F13.opExtrude","CAP_FACE",FACE,{"disambiguationData":[OSD([sQuery(id+"F9.wireOp",EDGE,"E154.MirrorCS"),sQuery(id+"F9.wireOp",EDGE,"E155.MirrorCS"),sQuery(id+"F9.wireOp",EDGE,"E156.MirrorCS"),sQuery(id+"F9.wireOp",EDGE,"E158.MirrorCS")])],"isStart":true});
            var Q1;
            Q1=makeQuery(id+"F13.opExtrude","CAP_FACE",FACE,{"disambiguationData":[OSD([sQuery(id+"F9.wireOp",EDGE,"E152.bottom"),sQuery(id+"F9.wireOp",EDGE,"E152.top"),sQuery(id+"F9.wireOp",EDGE,"E152.left"),sQuery(id+"F9.wireOp",EDGE,"E152.right")])],"isStart":true});
            extrude(context, id + "F15", {"entities" : qUnion([Q0, Q1]), "operationType" : NewBodyOperationType.ADD, "depth" : 107.5 * mm, "offsetDistance" : 25 * mm});
        }
        {
            var Q0;
            Q0=makeQuery(id+"F14.opExtrude","CAP_FACE",FACE,{"disambiguationData":[OSD([sQuery(id+"F9.wireOp",EDGE,"E152.bottom"),sQuery(id+"F9.wireOp",EDGE,"E152.top"),sQuery(id+"F9.wireOp",EDGE,"E152.left"),sQuery(id+"F9.wireOp",EDGE,"E152.right")])],"isStart":false});
            var sketch = newSketch(context, id + "F16", { "sketchPlane" : qUnion([Q0])});
            skLineSegment(sketch, "E177", {"start": v(-1600, -225) * mm, "end": v(-1600, -110) * mm, "construction": true});
            skLineSegment(sketch, "E178", {"start": v(-1675, -210) * mm, "end": v(-1525, -210) * mm, "construction": true});
            skArc(sketch, "E179", {"start": v(-1570, -210) * mm, "mid": v(-1600, -180) * mm, "end": v(-1630, -210) * mm});
            skLineSegment(sketch, "E180", {"start": v(-1630, -210) * mm, "end": v(-1632.5, -225) * mm});
            skLineSegment(sketch, "E181", {"start": v(-1570, -210) * mm, "end": v(-1567.5, -225) * mm});
            skLineSegment(sketch, "E182", {"start": v(-1632.5, -225) * mm, "end": v(-1567.5, -225) * mm});
            skArc(sketch, "E183.MirrorCS", {"start": v(1570, -210) * mm, "mid": v(1600, -180) * mm, "end": v(1630, -210) * mm});
            skLineSegment(sketch, "E184.MirrorCS", {"start": v(1570, -210) * mm, "end": v(1567.5, -225) * mm});
            skLineSegment(sketch, "E185.MirrorCS", {"start": v(1632.5, -225) * mm, "end": v(1567.5, -225) * mm});
            skLineSegment(sketch, "E186.MirrorCS", {"start": v(1630, -210) * mm, "end": v(1632.5, -225) * mm});
            skSolve(sketch);
        }
        {
            var Q0;
            Q0=makeQuery(id+"F16.imprint","IMPRINT",FACE,{"disambiguationData":[TD([[makeQuery(id+"F16.imprint","IMPRINT",EDGE,{"derivedFrom":sQuery(id+"F16.wireOp",EDGE,"E183.MirrorCS")}),-1.0]])]});
            var Q1;
            Q1=makeQuery(id+"F16.imprint","IMPRINT",FACE,{"disambiguationData":[TD([[makeQuery(id+"F16.imprint","IMPRINT",EDGE,{"derivedFrom":sQuery(id+"F16.wireOp",EDGE,"E179")}),1.0]])]});
            extrude(context, id + "F17", {"entities" : qUnion([Q0, Q1]), "operationType" : NewBodyOperationType.REMOVE, "endBound" : BoundingType.THROUGH_ALL, "oppositeDirection" : true, "depth" : 25 * mm, "offsetDistance" : 25 * mm});
        }
        {
            var Q0;
            {var subQ0=sQuery(id+"F9.wireOp",EDGE,"E152.right");var subQ2=sQuery(id+"F9.wireOp",EDGE,"E152.top");Q0=makeQuery(id+"F17.boolean.opBoolean","SPLIT",FACE,{"disambiguationData":[TD([makeQuery(id+"F13.opExtrude","SWEPT_FACE",FACE,{"disambiguationData":[OSD([subQ0])]})])],"derivedFrom":makeQuery(id+"F15.boolean.opBoolean","MERGE",FACE,{"derivedFrom":[makeQuery(id+"F14.boolean.opBoolean","MERGE",FACE,{"derivedFrom":[makeQuery(id+"F13.opExtrude","SWEPT_FACE",FACE,{"disambiguationData":[OSD([subQ2])]}),makeQuery(id+"F14.opExtrude","SWEPT_FACE",FACE,{"disambiguationData":[OSD([subQ2])]})]}),makeQuery(id+"F15.opExtrude","SWEPT_FACE",FACE,{"disambiguationData":[OSD([subQ2])]})]})});}
            var sketch = newSketch(context, id + "F18", { "sketchPlane" : qUnion([Q0])});
            skLineSegment(sketch, "E187.bottom", {"start": v(1525, 582.5) * mm, "end": v(1675, 582.5) * mm});
            skLineSegment(sketch, "E187.top", {"start": v(1525, 457.5) * mm, "end": v(1675, 457.5) * mm});
            skLineSegment(sketch, "E187.left", {"start": v(1525, 582.5) * mm, "end": v(1525, 457.5) * mm});
            skLineSegment(sketch, "E187.right", {"start": v(1675, 582.5) * mm, "end": v(1675, 457.5) * mm});
            skLineSegment(sketch, "E188.0", {"start": v(1675, 607.5) * mm, "end": v(1525, 607.5) * mm});
            skLineSegment(sketch, "E189.bottom", {"start": v(1675, 432.5) * mm, "end": v(1525, 432.5) * mm});
            skLineSegment(sketch, "E189.top", {"start": v(1675, -432.5) * mm, "end": v(1525, -432.5) * mm});
            skLineSegment(sketch, "E189.left", {"start": v(1675, 432.5) * mm, "end": v(1675, -432.5) * mm});
            skLineSegment(sketch, "E189.right", {"start": v(1525, 432.5) * mm, "end": v(1525, -432.5) * mm});
            skPoint(sketch, "E190", {"position": v(1525, 0) * mm});
            skLineSegment(sketch, "E191.MirrorCS", {"start": v(1525, -457.5) * mm, "end": v(1675, -457.5) * mm});
            skLineSegment(sketch, "E192.MirrorCS", {"start": v(1525, -582.5) * mm, "end": v(1525, -457.5) * mm});
            skLineSegment(sketch, "E193.MirrorCS", {"start": v(1675, -582.5) * mm, "end": v(1675, -457.5) * mm});
            skLineSegment(sketch, "E194.MirrorCS", {"start": v(1525, -582.5) * mm, "end": v(1675, -582.5) * mm});
            skLineSegment(sketch, "E195.MirrorCS", {"start": v(-1525, -582.5) * mm, "end": v(-1675, -582.5) * mm});
            skLineSegment(sketch, "E196.MirrorCS", {"start": v(-1525, -582.5) * mm, "end": v(-1525, -457.5) * mm});
            skLineSegment(sketch, "E197.MirrorCS", {"start": v(-1525, -457.5) * mm, "end": v(-1675, -457.5) * mm});
            skLineSegment(sketch, "E198.MirrorCS", {"start": v(-1675, -582.5) * mm, "end": v(-1675, -457.5) * mm});
            skLineSegment(sketch, "E199.MirrorCS", {"start": v(-1675, -432.5) * mm, "end": v(-1525, -432.5) * mm});
            skLineSegment(sketch, "E200.MirrorCS", {"start": v(-1525, 432.5) * mm, "end": v(-1525, -432.5) * mm});
            skLineSegment(sketch, "E201.MirrorCS", {"start": v(-1675, 432.5) * mm, "end": v(-1675, -432.5) * mm});
            skLineSegment(sketch, "E202.MirrorCS", {"start": v(-1525, 582.5) * mm, "end": v(-1675, 582.5) * mm});
            skLineSegment(sketch, "E203.MirrorCS", {"start": v(-1525, 582.5) * mm, "end": v(-1525, 457.5) * mm});
            skLineSegment(sketch, "E204.MirrorCS", {"start": v(-1525, 457.5) * mm, "end": v(-1675, 457.5) * mm});
            skLineSegment(sketch, "E205.MirrorCS", {"start": v(-1675, 582.5) * mm, "end": v(-1675, 457.5) * mm});
            skLineSegment(sketch, "E206.MirrorCS", {"start": v(-1675, 432.5) * mm, "end": v(-1525, 432.5) * mm});
            skSolve(sketch);
        }
        {
            var Q0;
            {var subQ0=sQuery(id+"F18.wireOp",EDGE,"E205.MirrorCS");Q0=makeQuery(id+"F18.imprint","IMPRINT",FACE,{"disambiguationData":[TD([[makeQuery(id+"F18.imprint","IMPRINT",EDGE,{"derivedFrom":subQ0}),1.0]])]});}
            var Q1;
            {var subQ0=sQuery(id+"F18.wireOp",EDGE,"E203.MirrorCS");Q1=makeQuery(id+"F18.imprint","IMPRINT",FACE,{"disambiguationData":[TD([[makeQuery(id+"F18.imprint","IMPRINT",EDGE,{"derivedFrom":subQ0}),-1.0]])]});}
            var Q2;
            {var subQ0=sQuery(id+"F18.wireOp",EDGE,"E201.MirrorCS");Q2=makeQuery(id+"F18.imprint","IMPRINT",FACE,{"disambiguationData":[TD([[makeQuery(id+"F18.imprint","IMPRINT",EDGE,{"derivedFrom":subQ0}),1.0]])]});}
            var Q3;
            {var subQ0=sQuery(id+"F18.wireOp",EDGE,"E200.MirrorCS");Q3=makeQuery(id+"F18.imprint","IMPRINT",FACE,{"disambiguationData":[TD([[makeQuery(id+"F18.imprint","IMPRINT",EDGE,{"derivedFrom":subQ0}),-1.0]])]});}
            var Q4;
            {var subQ0=sQuery(id+"F18.wireOp",EDGE,"E198.MirrorCS");Q4=makeQuery(id+"F18.imprint","IMPRINT",FACE,{"disambiguationData":[TD([[makeQuery(id+"F18.imprint","IMPRINT",EDGE,{"derivedFrom":subQ0}),-1.0]])]});}
            var Q5;
            {var subQ0=sQuery(id+"F18.wireOp",EDGE,"E196.MirrorCS");Q5=makeQuery(id+"F18.imprint","IMPRINT",FACE,{"disambiguationData":[TD([[makeQuery(id+"F18.imprint","IMPRINT",EDGE,{"derivedFrom":subQ0}),-1.0]])]});}
            var Q6;
            Q6=makeQuery(id+"F18.imprint","IMPRINT",FACE,{"disambiguationData":[TD([[makeQuery(id+"F18.imprint","IMPRINT",EDGE,{"derivedFrom":sQuery(id+"F18.wireOp",EDGE,"E187.bottom")}),-1.0]])]});
            var Q7;
            Q7=makeQuery(id+"F18.imprint","IMPRINT",FACE,{"disambiguationData":[TD([[makeQuery(id+"F18.imprint","IMPRINT",EDGE,{"derivedFrom":sQuery(id+"F18.wireOp",EDGE,"E189.bottom")}),1.0]])]});
            var Q8;
            Q8=makeQuery(id+"F18.imprint","IMPRINT",FACE,{"disambiguationData":[TD([[makeQuery(id+"F18.imprint","IMPRINT",EDGE,{"derivedFrom":sQuery(id+"F18.wireOp",EDGE,"E191.MirrorCS")}),-1.0]])]});
            var Q9;
            {var subQ0=sQuery(id+"F9.wireOp",EDGE,"E152.bottom");Q9=makeQuery(id+"F15.boolean.opBoolean","MERGE",FACE,{"derivedFrom":[makeQuery(id+"F14.boolean.opBoolean","MERGE",FACE,{"derivedFrom":[makeQuery(id+"F13.opExtrude","SWEPT_FACE",FACE,{"disambiguationData":[OSD([subQ0])]}),makeQuery(id+"F14.opExtrude","SWEPT_FACE",FACE,{"disambiguationData":[OSD([subQ0])]})]}),makeQuery(id+"F15.opExtrude","SWEPT_FACE",FACE,{"disambiguationData":[OSD([subQ0])]})]});}
            extrude(context, id + "F19", {"entities" : qUnion([Q0, Q1, Q2, Q3, Q4, Q5, Q6, Q7, Q8]), "operationType" : NewBodyOperationType.REMOVE, "endBound" : BoundingType.UP_TO_SURFACE, "oppositeDirection" : true, "depth" : 25 * mm, "endBoundEntityFace" : qUnion([Q9]), "offsetDistance" : 25 * mm});
        }
    });
